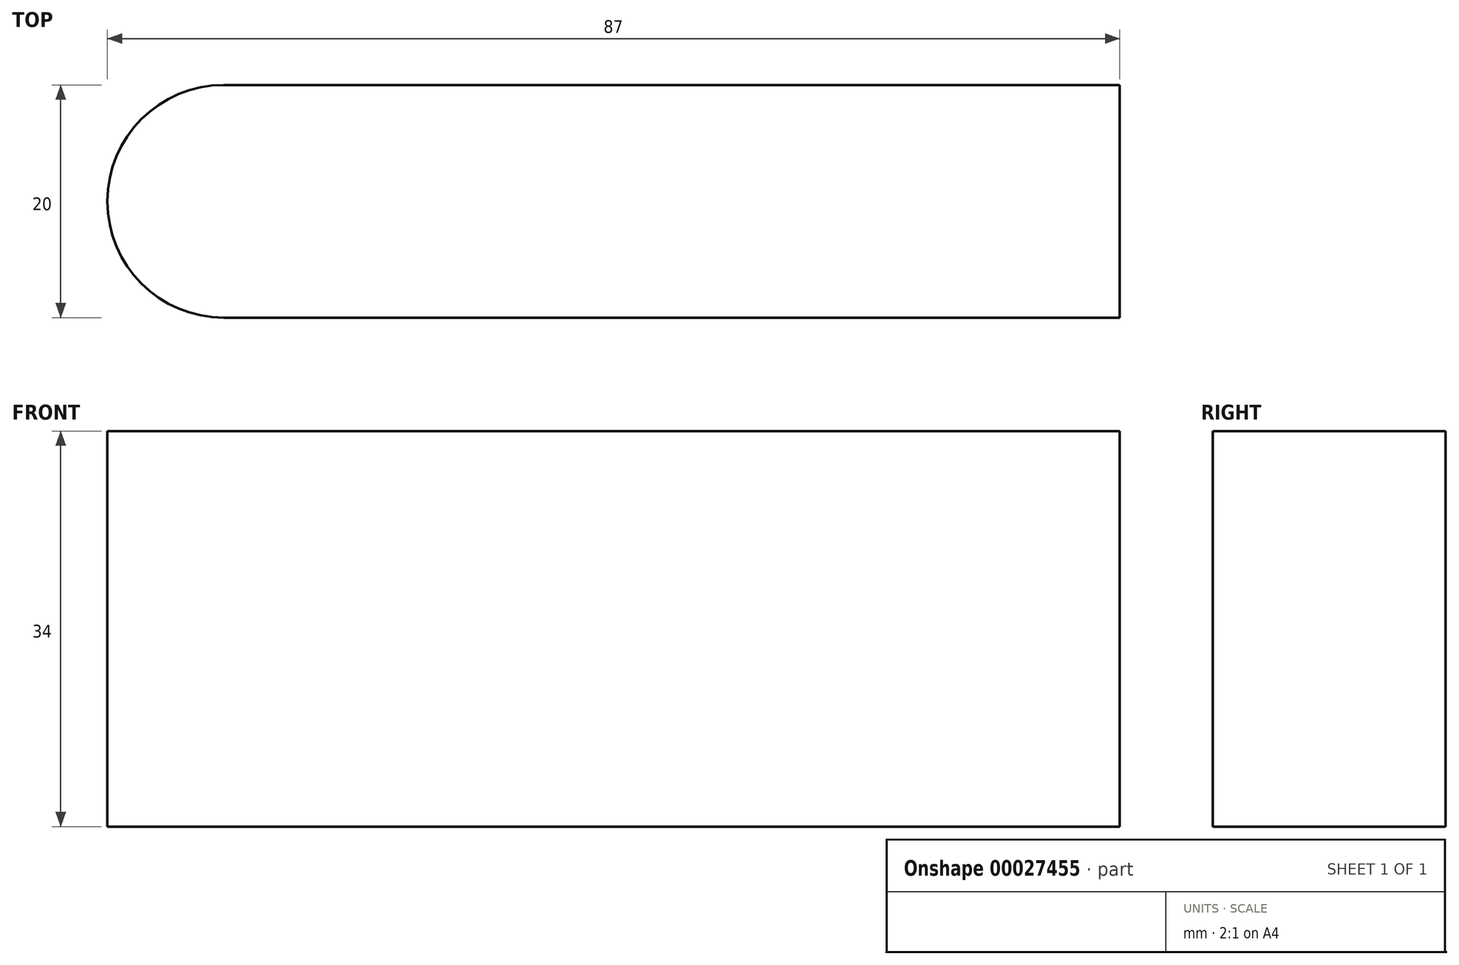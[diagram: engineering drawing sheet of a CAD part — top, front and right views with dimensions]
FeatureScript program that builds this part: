
annotation { "Feature Type Name" : "Feature", "Feature Type Description" : "" }
export const myFeature = defineFeature(function(context is Context, id is Id, definition is map)
    precondition{}
    {
        {
            var Q0;
            Q0=qCreatedBy(makeId("Top.planeOp"),FACE);
            var sketch = newSketch(context, id + "F0", { "sketchPlane" : qUnion([Q0])});
            skLineSegment(sketch, "E0.rect.bottom", {"start": v(-33.5, 10) * mm, "end": v(43.5, 10) * mm});
            skLineSegment(sketch, "E0.rect.top", {"start": v(-33.5, -10) * mm, "end": v(43.5, -10) * mm});
            skLineSegment(sketch, "E0.rect.left", {"start": v(-43.5, 0) * mm, "end": v(-43.5, 0) * mm});
            skLineSegment(sketch, "E0.rect.right", {"start": v(43.5, 10) * mm, "end": v(43.5, -10) * mm});
            skPoint(sketch, "E0.rect.middle", {"position": v(0, 0) * mm});
            skPoint(sketch, "E1.visualSharp", {"position": v(-43.5, 10) * mm});
            skArc(sketch, "E1.filletArc", {"start": v(-33.5, 10) * mm, "mid": v(-40.57, 7.07) * mm, "end": v(-43.5, 0) * mm});
            skPoint(sketch, "E2.visualSharp", {"position": v(-43.5, -10) * mm});
            skArc(sketch, "E2.filletArc", {"start": v(-43.5, 0) * mm, "mid": v(-40.57, -7.07) * mm, "end": v(-33.5, -10) * mm});
            skSolve(sketch);
        }
        {
            var Q0;
            Q0=makeQuery(id+"F0.imprint","IMPRINT",FACE,{"disambiguationData":[TD([[makeQuery(id+"F0.imprint","IMPRINT",EDGE,{"derivedFrom":sQuery(id+"F0.wireOp",EDGE,"E0.rect.bottom")}),-1.0]])]});
            extrude(context, id + "F1", {"entities" : qUnion([Q0]), "depth" : 34 * mm});
        }
    });
